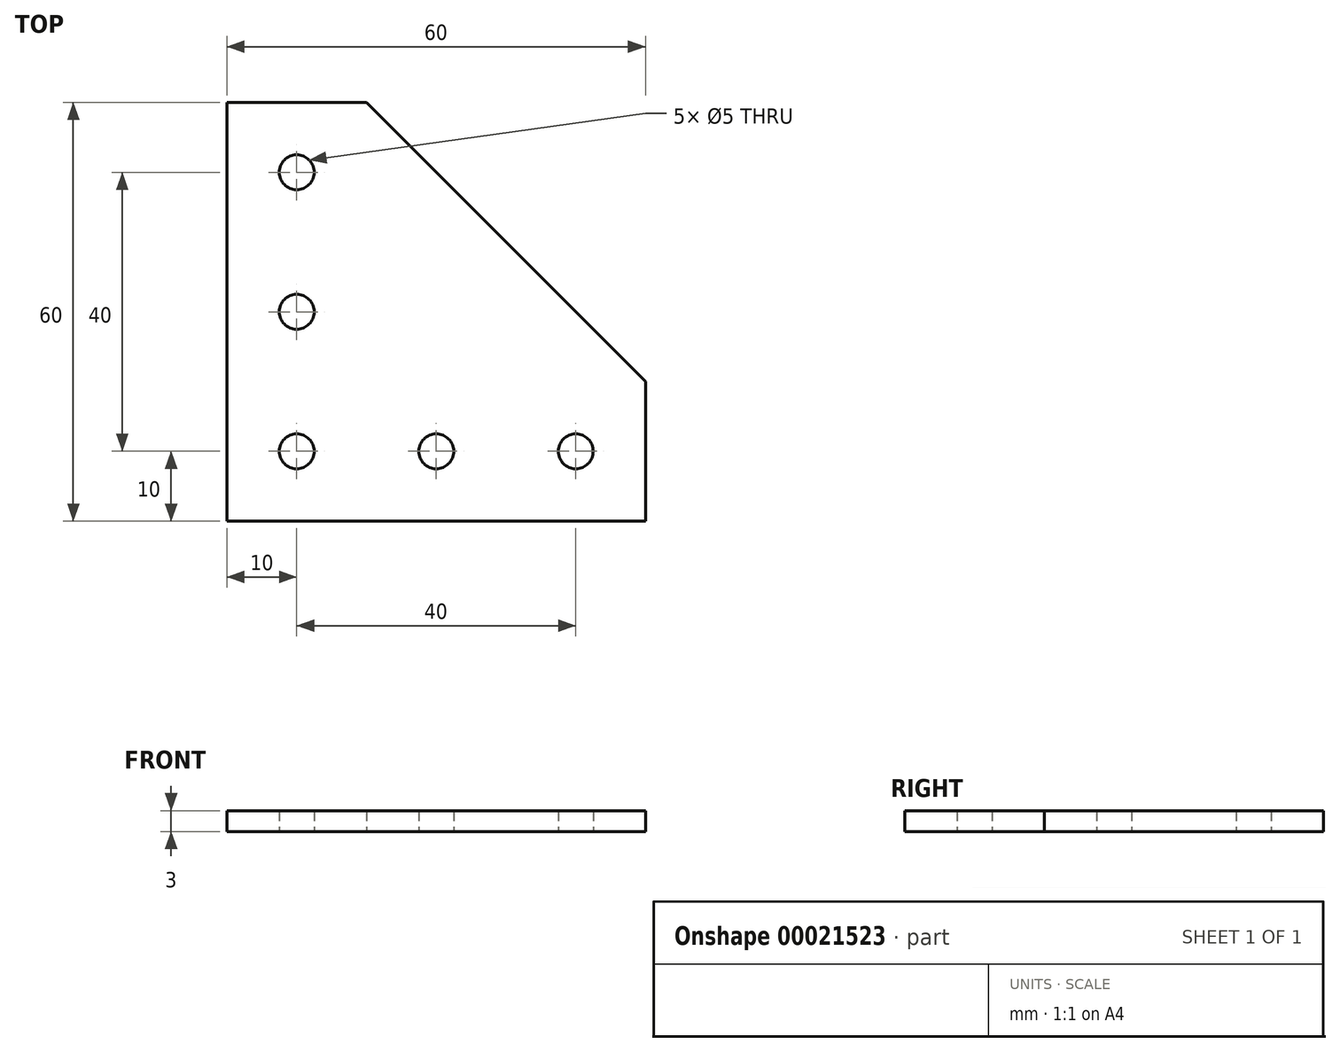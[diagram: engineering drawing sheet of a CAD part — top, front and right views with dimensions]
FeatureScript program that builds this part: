
annotation { "Feature Type Name" : "Feature", "Feature Type Description" : "" }
export const myFeature = defineFeature(function(context is Context, id is Id, definition is map)
    precondition{}
    {
        {
            var Q0;
            Q0=qCreatedBy(makeId("Top.planeOp"),FACE);
            var sketch = newSketch(context, id + "F0", { "sketchPlane" : qUnion([Q0])});
            skLineSegment(sketch, "E0.rect.bottom", {"start": v(30, -30) * mm, "end": v(-30, -30) * mm});
            skLineSegment(sketch, "E0.rect.top", {"start": v(-10, 30) * mm, "end": v(-30, 30) * mm});
            skLineSegment(sketch, "E0.rect.left", {"start": v(30, -30) * mm, "end": v(30, -10) * mm});
            skLineSegment(sketch, "E0.rect.right", {"start": v(-30, -30) * mm, "end": v(-30, 30) * mm});
            skPoint(sketch, "E0.rect.middle", {"position": v(0, 0) * mm});
            skLineSegment(sketch, "E1", {"start": v(-10, 30) * mm, "end": v(30, -10) * mm});
            skPoint(sketch, "E2.orphan", {"position": v(30, 30) * mm});
            skPoint(sketch, "E3", {"position": v(-20, -20) * mm});
            skCircle(sketch, "E4", {"center": v(-20, -20) * mm, "radius": 2.5 * mm});
            skCircle(sketch, "E5.1.0.0", {"center": v(0, -20) * mm, "radius": 2.5 * mm});
            skCircle(sketch, "E5.2.0.0", {"center": v(20, -20) * mm, "radius": 2.5 * mm});
            skLineSegment(sketch, "E5.direction1", {"start": v(-20, -20) * mm, "end": v(-17.5, -20) * mm, "construction": true});
            skCircle(sketch, "E6.0.1.0", {"center": v(-20, 0) * mm, "radius": 2.5 * mm});
            skCircle(sketch, "E6.0.2.0", {"center": v(-20, 20) * mm, "radius": 2.5 * mm});
            skLineSegment(sketch, "E6.direction2", {"start": v(-20, -20) * mm, "end": v(-20, -17.5) * mm, "construction": true});
            skPoint(sketch, "E7.start.orphan", {"position": v(-30, -10) * mm});
            skLineSegment(sketch, "E8.trimOffspring", {"start": v(-2.5, -20) * mm, "end": v(2.5, -20) * mm, "construction": true});
            skLineSegment(sketch, "E9.trimOffspring", {"start": v(-20, -2.5) * mm, "end": v(-20, 0) * mm, "construction": true});
            skLineSegment(sketch, "E10.trimOffspring", {"start": v(-2.5, -20) * mm, "end": v(0, -20) * mm, "construction": true});
            skSolve(sketch);
        }
        {
            var Q0;
            Q0=makeQuery(id+"F0.imprint","IMPRINT",FACE,{"disambiguationData":[TD([[makeQuery(id+"F0.imprint","IMPRINT",EDGE,{"derivedFrom":sQuery(id+"F0.wireOp",EDGE,"E0.rect.bottom")}),-1.0]])]});
            extrude(context, id + "F1", {"entities" : qUnion([Q0]), "depth" : 3 * mm});
        }
    });
